# Revit family: Cistern_InWall_Nero_RandT
name_source: partatom
category: Plumbing Fixtures
units: mm (PartAtom-declared; Revit-internal decimal feet)

## family parameters
Always vertical = Yes
Cut with Voids When Loaded = Yes
Maintain Annotation Orientation = No
OmniClass Number = 23.31.00.00
OmniClass Title = Plumbing Specific Products and Equipment
Part Type = Normal
Room Calculation Point = No
Round Connector Dimension = Use Diameter
Shared = No
Work Plane-Based = No

## types (1)
- G30033
    Assembly Code = D2010
    CW Connection = Yes
    CWFU = 0
    Default Elevation = 1050 mm
    Description = R&T in-Wall Cistern
    HW Connection = No
    HWFU = 0
    IfcExportAs = IfcSanitaryTerminal
    IfcExportType = CISTERN
    Manufacturer = Nero
    ManufacturerOverallDepth = 172 mm
    ManufacturerOverallHeight = 992.5 mm
    ManufacturerOverallWidth = 551 mm  [stored 1.80774 ft]
    ManufacturerSpecCode = G30033
    ManufacturerURLProductSpecific = https://nerotapware.com.au
    Material = Metal_Nickel_Nero_Brushed
    Model = G30033
    ModifiedIssue = 20251105 $
    Type Comments = Hospital pattern WC pans and cisterns - In Wall - Brushed Nickel
    URL = https://nerotapware.com.au
    Uniclass2015Code = Pr_40_20_93_89
    Uniclass2015Title = WC cisterns
    Uniclass2015Version = Products v1.35
    Vent Connection = No
    WFU = 0
    Waste Connection = No

note: [stored X ft] marks values corroborated as IEEE doubles in the binary element streams (Revit-internal decimal feet)

## geometry (parser evidence)
native form markers: Sweep x2
no freeform markers — native parametric forms only
